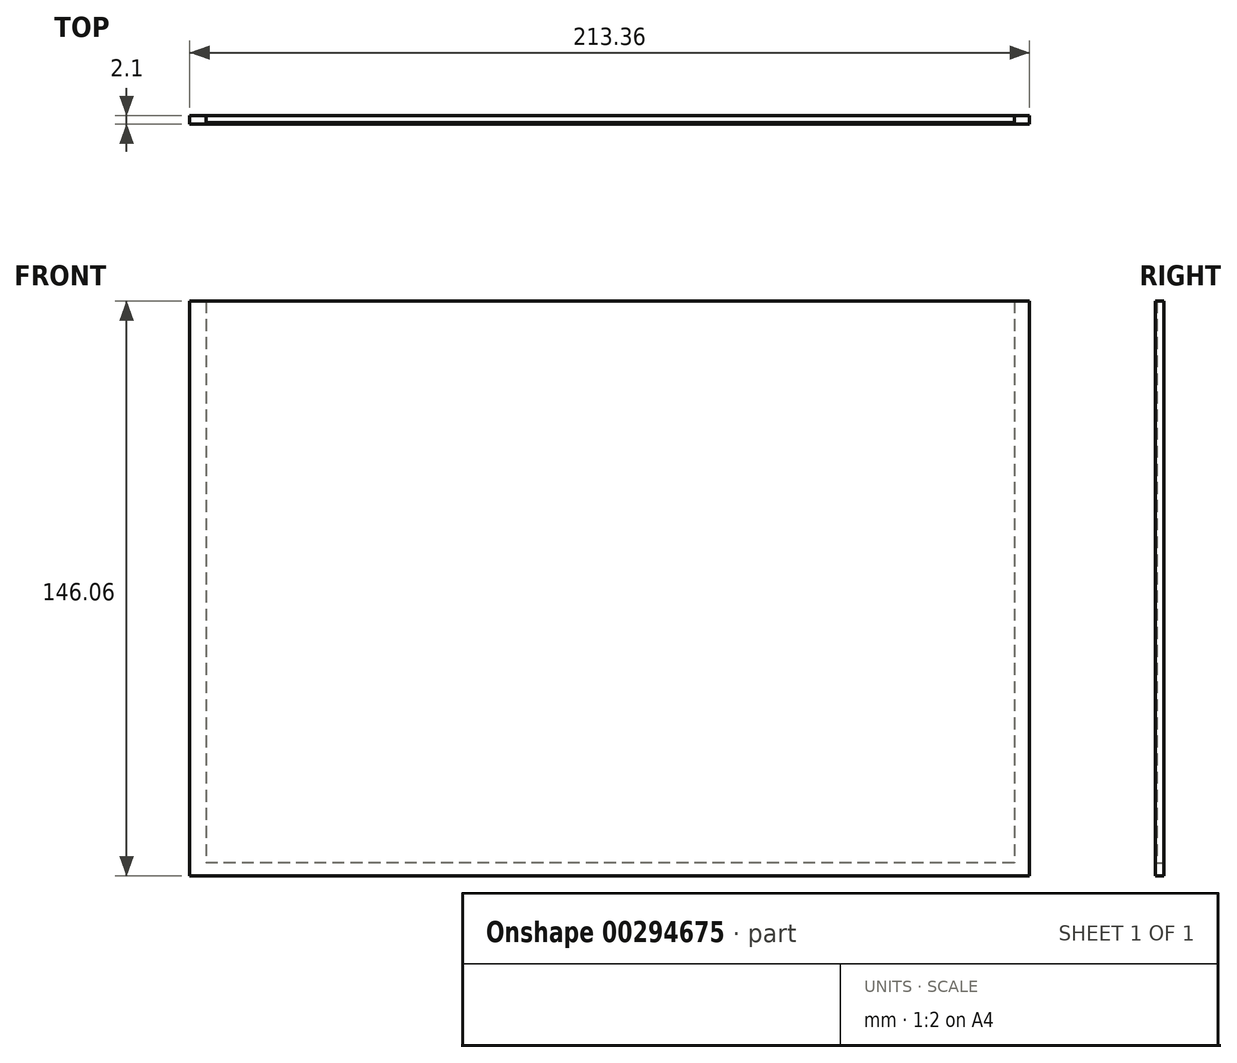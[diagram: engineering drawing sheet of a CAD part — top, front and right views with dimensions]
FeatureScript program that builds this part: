
annotation { "Feature Type Name" : "Feature", "Feature Type Description" : "" }
export const myFeature = defineFeature(function(context is Context, id is Id, definition is map)
    precondition{}
    {
        {
            var Q0;
            Q0=qCreatedBy(makeId("Front.planeOp"),FACE);
            var sketch = newSketch(context, id + "F0", { "sketchPlane" : qUnion([Q0])});
            skLineSegment(sketch, "E0.bottom", {"start": v(-106.68, 73.03) * mm, "end": v(106.68, 73.03) * mm});
            skLineSegment(sketch, "E0.top", {"start": v(-106.68, -73.03) * mm, "end": v(106.68, -73.03) * mm});
            skLineSegment(sketch, "E0.left", {"start": v(-106.68, 73.03) * mm, "end": v(-106.68, -73.02) * mm});
            skLineSegment(sketch, "E0.right", {"start": v(106.68, 73.03) * mm, "end": v(106.68, -73.02) * mm});
            skPoint(sketch, "E0.middle", {"position": v(0, 0) * mm});
            skSolve(sketch);
        }
        {
            var Q0;
            Q0=makeQuery(id+"F0.imprint","IMPRINT",FACE,{"disambiguationData":[TD([[makeQuery(id+"F0.imprint","IMPRINT",EDGE,{"derivedFrom":sQuery(id+"F0.wireOp",EDGE,"E0.bottom")}),-1.0]])]});
            extrude(context, id + "F1", {"entities" : qUnion([Q0]), "endBound" : BoundingType.SYMMETRIC, "depth" : 2.1 * mm});
        }
        {
            var Q0;
            Q0=makeQuery(id+"F1.opExtrude","CAP_FACE",FACE,{"disambiguationData":[OSD([sQuery(id+"F0.wireOp",EDGE,"E0.bottom"),sQuery(id+"F0.wireOp",EDGE,"E0.top"),sQuery(id+"F0.wireOp",EDGE,"E0.left"),sQuery(id+"F0.wireOp",EDGE,"E0.right")])],"isStart":true});
            var sketch = newSketch(context, id + "F2", { "sketchPlane" : qUnion([Q0])});
            skSolve(sketch);
        }
        {
            var Q0;
            Q0=makeQuery(id+"F2.imprint","IMPRINT",FACE,{"disambiguationData":[TD([[makeQuery(id+"F2.imprint","IMPRINT",EDGE,{"derivedFrom":makeQuery(id+"F1.opExtrude","CAP_EDGE",EDGE,{"disambiguationData":[OSD([sQuery(id+"F0.wireOp",EDGE,"E0.bottom")])],"isStart":true})}),1.0]])]});
            var sketch = newSketch(context, id + "F3", { "sketchPlane" : qUnion([Q0])});
            skLineSegment(sketch, "E1.bottom", {"start": v(-102.8, 73.73) * mm, "end": v(102.56, 73.73) * mm});
            skLineSegment(sketch, "E1.top", {"start": v(-102.8, -69.78) * mm, "end": v(102.56, -69.78) * mm});
            skLineSegment(sketch, "E1.left", {"start": v(-102.8, 73.73) * mm, "end": v(-102.8, -69.78) * mm});
            skLineSegment(sketch, "E1.right", {"start": v(102.56, 73.73) * mm, "end": v(102.56, -69.78) * mm});
            skSolve(sketch);
        }
        {
            var Q0;
            Q0 = qSketchRegion(id + "F3", true);
            extrude(context, id + "F4", {"entities" : qUnion([Q0]), "operationType" : NewBodyOperationType.REMOVE, "oppositeDirection" : true, "depth" : 1.78 * mm});
        }
    });
